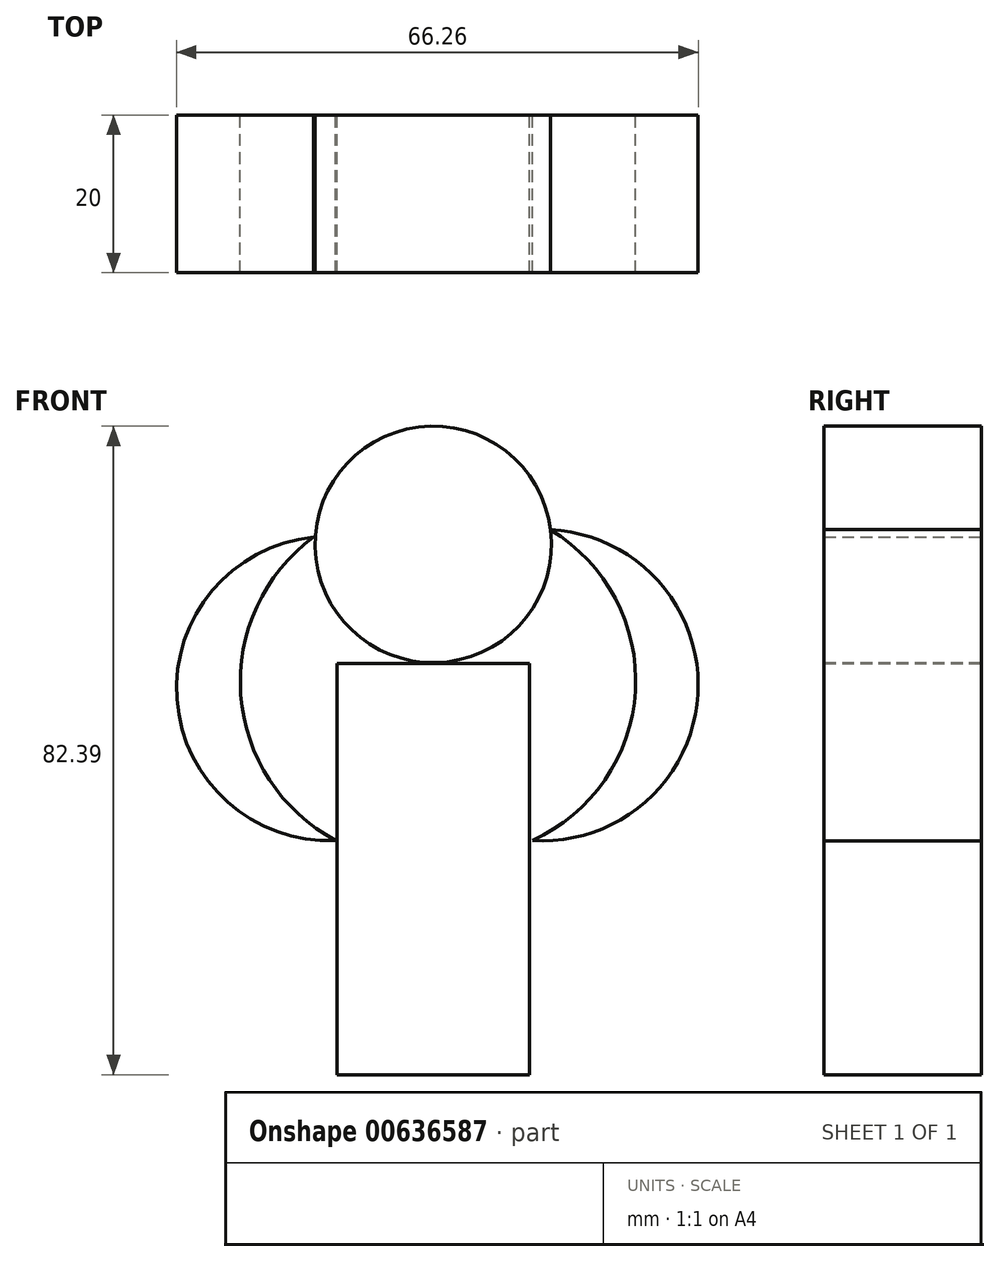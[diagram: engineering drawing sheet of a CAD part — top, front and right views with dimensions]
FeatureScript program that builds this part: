
annotation { "Feature Type Name" : "Feature", "Feature Type Description" : "" }
export const myFeature = defineFeature(function(context is Context, id is Id, definition is map)
    precondition{}
    {
        {
            var Q0;
            Q0=qCreatedBy(makeId("Front.planeOp"),FACE);
            var sketch = newSketch(context, id + "F0", { "sketchPlane" : qUnion([Q0])});
            skCircle(sketch, "E0", {"center": v(0, 37.6) * mm, "radius": 15.02 * mm});
            skSolve(sketch);
        }
        {
            var Q0;
            Q0=makeQuery(id+"F0.imprint","IMPRINT",FACE,{"disambiguationData":[TD([[makeQuery(id+"F0.imprint","IMPRINT",EDGE,{"derivedFrom":sQuery(id+"F0.wireOp",EDGE,"E0")}),1.0]])]});
            extrude(context, id + "F1", {"entities" : qUnion([Q0]), "depth" : 20 * mm, "offsetDistance" : 25 * mm});
        }
        {
            var Q0;
            Q0=qCreatedBy(makeId("Front.planeOp"),FACE);
            var sketch = newSketch(context, id + "F2", { "sketchPlane" : qUnion([Q0])});
            skLineSegment(sketch, "E1.bottom", {"start": v(-12.22, 22.49) * mm, "end": v(12.22, 22.49) * mm});
            skLineSegment(sketch, "E1.top", {"start": v(-12.22, -29.76) * mm, "end": v(12.22, -29.76) * mm});
            skLineSegment(sketch, "E1.left", {"start": v(-12.22, 22.49) * mm, "end": v(-12.22, -29.76) * mm});
            skLineSegment(sketch, "E1.right", {"start": v(12.22, 22.49) * mm, "end": v(12.22, -29.76) * mm});
            skSolve(sketch);
        }
        {
            var Q0;
            Q0=makeQuery(id+"F2.imprint","IMPRINT",FACE,{"disambiguationData":[TD([[makeQuery(id+"F2.imprint","IMPRINT",EDGE,{"derivedFrom":sQuery(id+"F2.wireOp",EDGE,"E1.bottom")}),-1.0]])]});
            extrude(context, id + "F3", {"entities" : qUnion([Q0]), "depth" : 20 * mm, "offsetDistance" : 25 * mm});
        }
        {
            var Q0;
            Q0=qCreatedBy(makeId("Front.planeOp"),FACE);
            var sketch = newSketch(context, id + "F4", { "sketchPlane" : qUnion([Q0])});
            skArc(sketch, "E2", {"start": v(12.6, 0) * mm, "mid": v(33.63, 18.6) * mm, "end": v(14.84, 39.47) * mm});
            skArc(sketch, "E3", {"start": v(12.6, 0) * mm, "mid": v(25.68, 19.06) * mm, "end": v(14.84, 39.47) * mm});
            skSolve(sketch);
        }
        {
            var Q0;
            Q0=makeQuery(id+"F4.imprint","IMPRINT",FACE,{"disambiguationData":[TD([[makeQuery(id+"F4.imprint","IMPRINT",EDGE,{"derivedFrom":sQuery(id+"F4.wireOp",EDGE,"E2")}),1.0]])]});
            extrude(context, id + "F5", {"entities" : qUnion([Q0]), "operationType" : NewBodyOperationType.ADD, "depth" : 20 * mm, "offsetDistance" : 25 * mm});
        }
        {
            var Q0;
            Q0=qCreatedBy(makeId("Front.planeOp"),FACE);
            var sketch = newSketch(context, id + "F6", { "sketchPlane" : qUnion([Q0])});
            skArc(sketch, "E4", {"start": v(-15.2, 38.54) * mm, "mid": v(-32.55, 17.9) * mm, "end": v(-12.4, 0) * mm});
            skArc(sketch, "E5", {"start": v(-15.2, 38.54) * mm, "mid": v(-24.44, 18.5) * mm, "end": v(-12.4, 0) * mm});
            skSolve(sketch);
        }
        {
            var Q0;
            Q0 = qSketchRegion(id + "F6", true);
            extrude(context, id + "F7", {"entities" : qUnion([Q0]), "depth" : 20 * mm, "offsetDistance" : 25 * mm});
        }
    });
